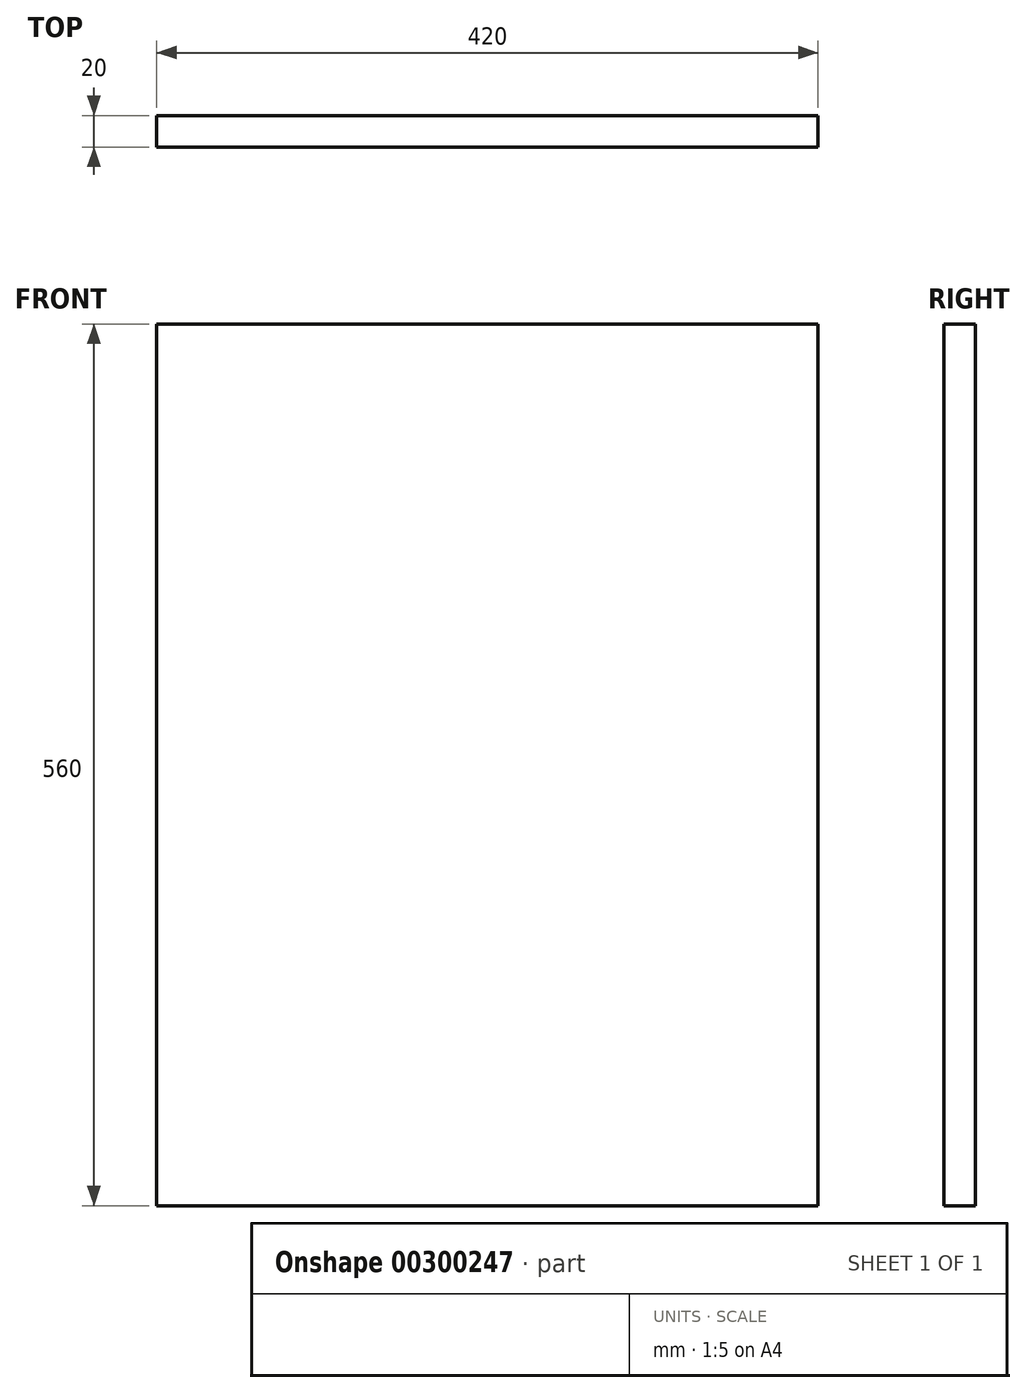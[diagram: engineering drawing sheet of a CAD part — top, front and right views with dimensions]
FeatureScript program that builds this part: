
annotation { "Feature Type Name" : "Feature", "Feature Type Description" : "" }
export const myFeature = defineFeature(function(context is Context, id is Id, definition is map)
    precondition{}
    {
        {
            var Q0;
            Q0=qCreatedBy(makeId("Front.planeOp"),FACE);
            var sketch = newSketch(context, id + "F0", { "sketchPlane" : qUnion([Q0])});
            skLineSegment(sketch, "E0.bottom", {"start": v(-210, 280) * mm, "end": v(210, 280) * mm});
            skLineSegment(sketch, "E0.top", {"start": v(-210, -280) * mm, "end": v(210, -280) * mm});
            skLineSegment(sketch, "E0.left", {"start": v(-210, 280) * mm, "end": v(-210, -280) * mm});
            skLineSegment(sketch, "E0.right", {"start": v(210, 280) * mm, "end": v(210, -280) * mm});
            skPoint(sketch, "E0.middle", {"position": v(0, 0) * mm});
            skSolve(sketch);
        }
        {
            var Q0;
            Q0=makeQuery(id+"F0.imprint","IMPRINT",FACE,{"disambiguationData":[TD([[makeQuery(id+"F0.imprint","IMPRINT",EDGE,{"derivedFrom":sQuery(id+"F0.wireOp",EDGE,"E0.bottom")}),-1.0]])]});
            extrude(context, id + "F1", {"entities" : qUnion([Q0]), "depth" : 20 * mm});
        }
    });
